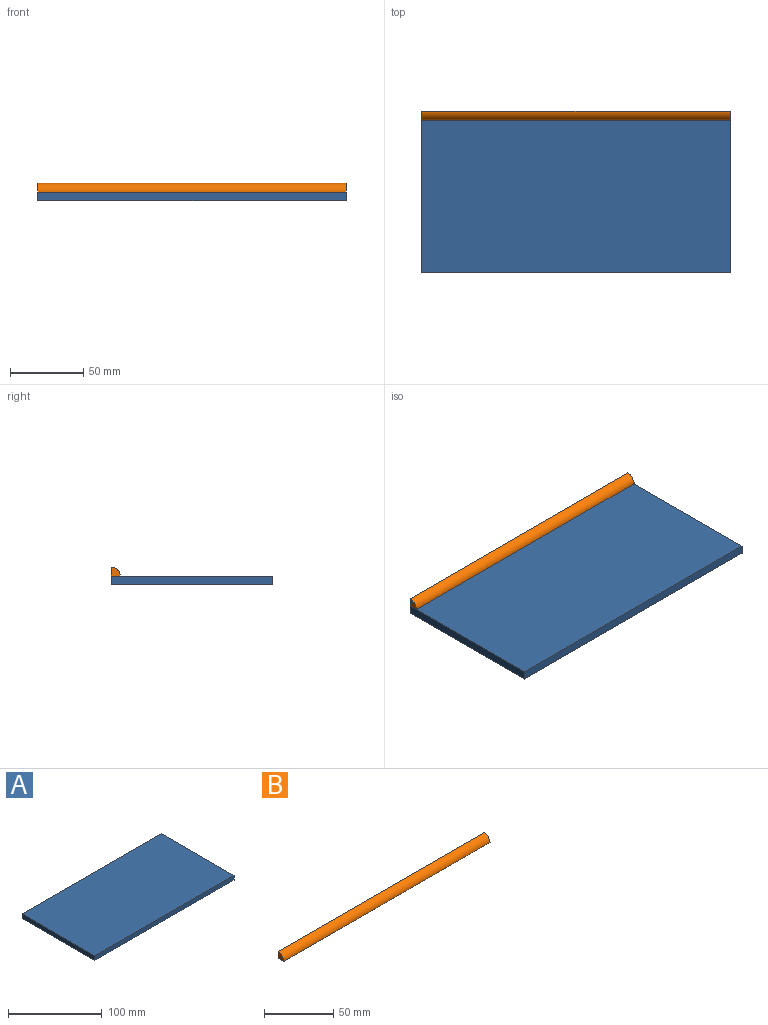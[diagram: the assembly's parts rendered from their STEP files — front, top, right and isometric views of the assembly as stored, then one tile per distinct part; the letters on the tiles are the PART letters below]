
ASSEMBLY  parts=2 mates=1
PART A: 6 faces, bbox 210x110x6 mm
  f0: plane 110x6mm, normal (1,0,0), area 660mm2, adj f1,f3,f4,f5
  f1: plane 210x6mm, normal (0,1,0), area 1260mm2, adj f0,f2,f4,f5
  f2: plane 110x6mm, normal (-1,0,0), area 660mm2, adj f1,f3,f4,f5
  f3: plane 210x6mm, normal (0,-1,0), area 1260mm2, adj f0,f2,f4,f5
  f4: plane 210x110mm, normal (0,0,1), area 23100mm2, adj f0,f1,f2,f3
  f5: plane 210x110mm, normal (0,0,-1), area 23100mm2, adj f0,f1,f2,f3
PART B: 5 faces, bbox 210x6x6 mm
  f0: plane 210x6mm, normal (0,0,-1), area 1260mm2, adj f1,f2,f3,f4
  f1: plane 210x6mm, normal (0,1,0), area 1260mm2, adj f0,f2,f3,f4
  f2: cylinder r=6mm len=210mm, axis (-1,0,0), area 1979.2mm2, adj f0,f1,f3,f4
  f3: plane 6x6mm, normal (1,0,0), area 28.3mm2, adj f0,f1,f2
  f4: plane 6x6mm, normal (-1,0,0), area 28.3mm2, adj f0,f1,f2
PLACE A t=(-0.05,0.08,-2.84)mm
PLACE B t=(-105.05,59.01,3.16)mm
MATE fastened B.f0 <-> A.f4  axis (0,0,1) through (104.95,55.08,3.16)mm
